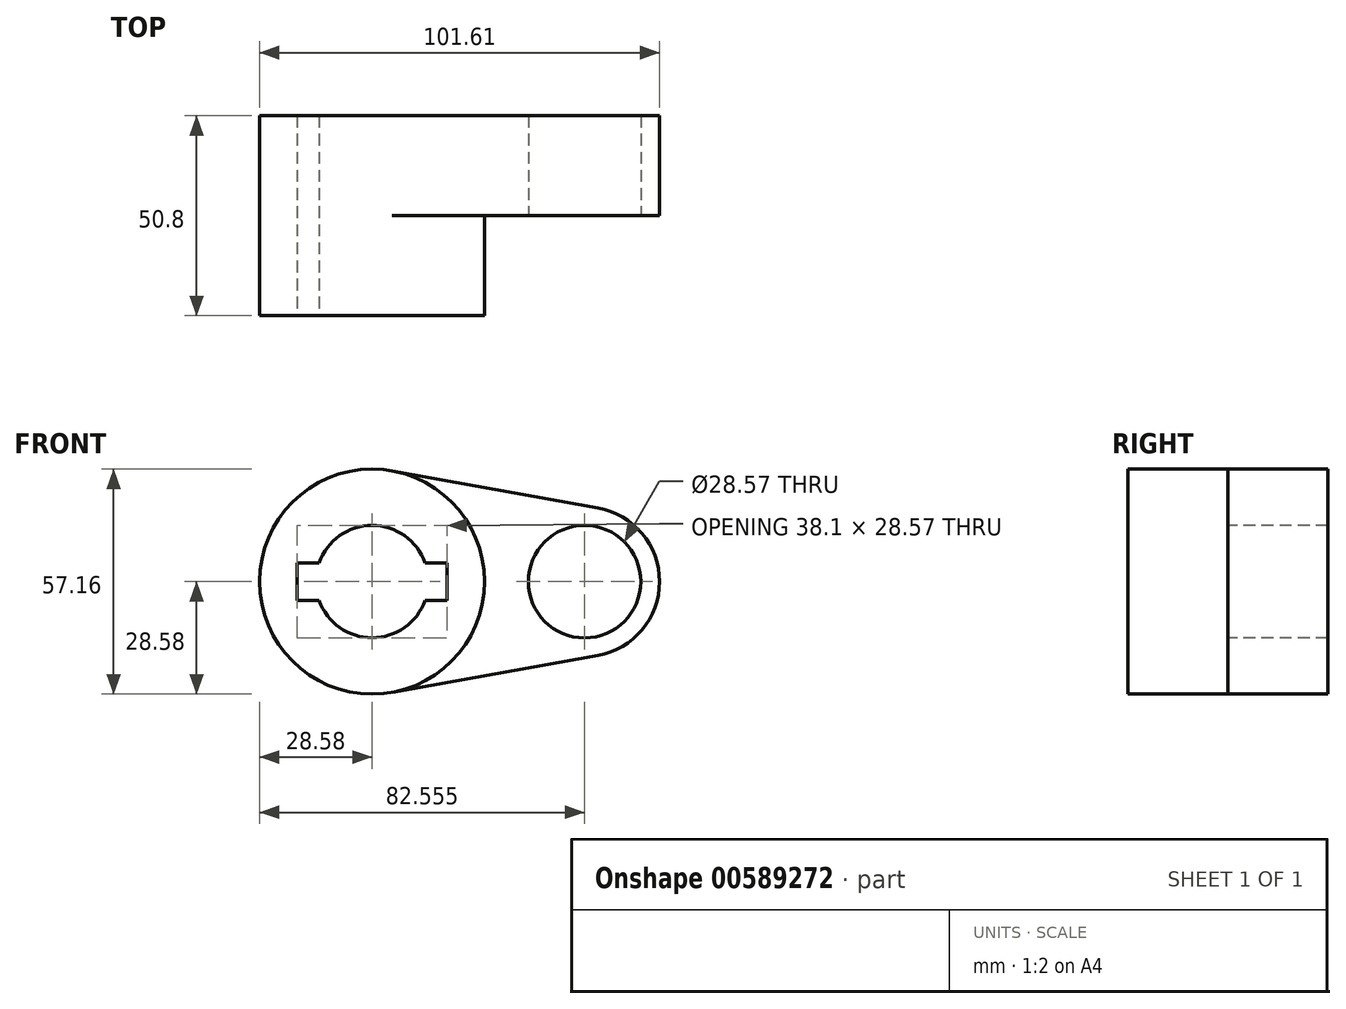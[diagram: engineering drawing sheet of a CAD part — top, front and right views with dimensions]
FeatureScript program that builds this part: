
annotation { "Feature Type Name" : "Feature", "Feature Type Description" : "" }
export const myFeature = defineFeature(function(context is Context, id is Id, definition is map)
    precondition{}
    {
        {
            var Q0;
            Q0=qCreatedBy(makeId("Front.planeOp"),FACE);
            var sketch = newSketch(context, id + "F0", { "sketchPlane" : qUnion([Q0])});
            skCircle(sketch, "E0", {"center": v(0, 0) * mm, "radius": 28.58 * mm});
            skCircle(sketch, "E1", {"center": v(53.98, 0) * mm, "radius": 19.05 * mm});
            skLineSegment(sketch, "E2", {"start": v(5.04, 28.13) * mm, "end": v(57.34, 18.75) * mm});
            skLineSegment(sketch, "E3", {"start": v(5.04, -28.13) * mm, "end": v(57.34, -18.75) * mm});
            skCircle(sketch, "E4", {"center": v(0, 0) * mm, "radius": 14.29 * mm});
            skCircle(sketch, "E5", {"center": v(53.98, 0) * mm, "radius": 14.29 * mm});
            skLineSegment(sketch, "E6.bottom", {"start": v(-19.05, 4.76) * mm, "end": v(19.05, 4.76) * mm});
            skLineSegment(sketch, "E6.top", {"start": v(-19.05, -4.76) * mm, "end": v(19.05, -4.76) * mm});
            skLineSegment(sketch, "E6.left", {"start": v(-19.05, 4.76) * mm, "end": v(-19.05, -4.76) * mm});
            skLineSegment(sketch, "E6.right", {"start": v(19.05, 4.76) * mm, "end": v(19.05, -4.76) * mm});
            skSolve(sketch);
        }
        {
            var Q0;
            {var subQ7=sQuery(id+"F0.wireOp",EDGE,"E6.left");Q0=makeQuery(id+"F0.imprint","IMPRINT",FACE,{"disambiguationData":[TD([[makeQuery(id+"F0.imprint","IMPRINT",EDGE,{"derivedFrom":subQ7}),-1.0]])]});}
            var Q1;
            Q1=makeQuery(id+"F0.imprint","IMPRINT",FACE,{"disambiguationData":[TD([[makeQuery(id+"F0.imprint","IMPRINT",EDGE,{"derivedFrom":sQuery(id+"F0.wireOp",EDGE,"E5")}),-1.0]])]});
            var Q2;
            {var subQ0=sQuery(id+"F0.wireOp",EDGE,"E2");Q2=makeQuery(id+"F0.imprint","IMPRINT",FACE,{"disambiguationData":[TD([[makeQuery(id+"F0.imprint","IMPRINT",EDGE,{"derivedFrom":subQ0}),-1.0]])]});}
            extrude(context, id + "F1", {"entities" : qUnion([Q0, Q1, Q2]), "oppositeDirection" : true, "depth" : 25.4 * mm, "offsetDistance" : 25.4 * mm});
        }
        {
            var Q0;
            {var subQ7=sQuery(id+"F0.wireOp",EDGE,"E6.left");Q0=makeQuery(id+"F0.imprint","IMPRINT",FACE,{"disambiguationData":[TD([[makeQuery(id+"F0.imprint","IMPRINT",EDGE,{"derivedFrom":subQ7}),-1.0]])]});}
            extrude(context, id + "F2", {"entities" : qUnion([Q0]), "operationType" : NewBodyOperationType.ADD, "depth" : 25.4 * mm, "offsetDistance" : 25.4 * mm});
        }
    });
